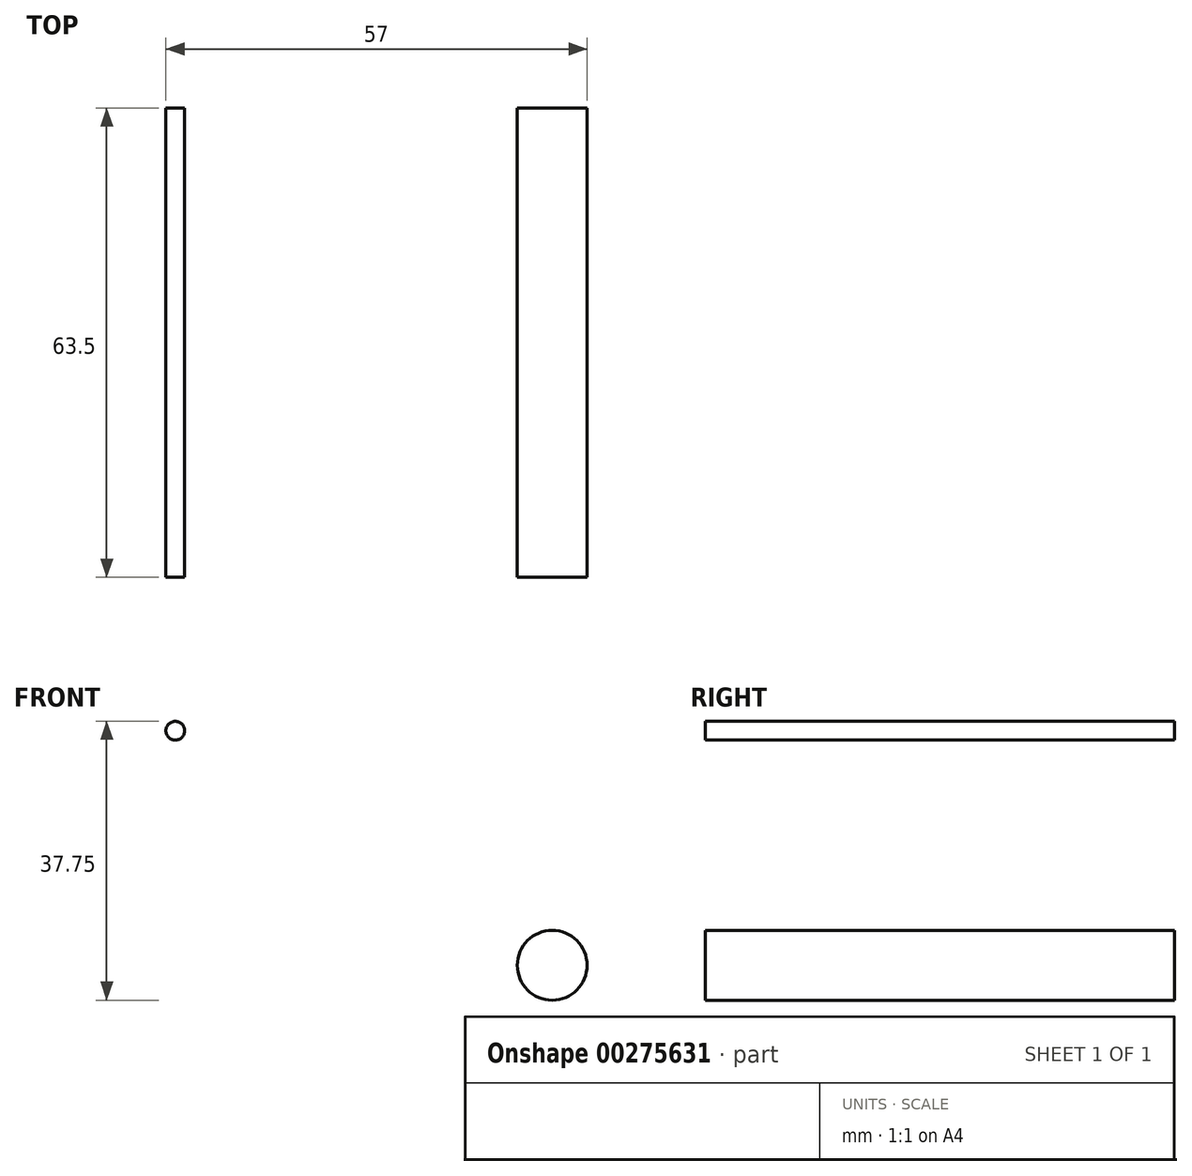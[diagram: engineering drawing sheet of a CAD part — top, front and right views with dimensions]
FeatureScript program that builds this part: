
annotation { "Feature Type Name" : "Feature", "Feature Type Description" : "" }
export const myFeature = defineFeature(function(context is Context, id is Id, definition is map)
    precondition{}
    {
        {
            var Q0;
            Q0=qCreatedBy(makeId("Front.planeOp"),FACE);
            var sketch = newSketch(context, id + "F0", { "sketchPlane" : qUnion([Q0])});
            skCircle(sketch, "E0", {"center": v(0, 0) * mm, "radius": 4.73 * mm});
            skSolve(sketch);
        }
        {
            var Q0;
            Q0=makeQuery(id+"F0.imprint","IMPRINT",FACE,{"disambiguationData":[TD([[makeQuery(id+"F0.imprint","IMPRINT",EDGE,{"derivedFrom":sQuery(id+"F0.wireOp",EDGE,"E0")}),1.0]])]});
            extrude(context, id + "F1", {"entities" : qUnion([Q0]), "depth" : 63.5 * mm});
        }
        {
            var Q0;
            Q0=qCreatedBy(makeId("Front.planeOp"),FACE);
            var sketch = newSketch(context, id + "F2", { "sketchPlane" : qUnion([Q0])});
            skCircle(sketch, "E1", {"center": v(-51, 31.75) * mm, "radius": 1.27 * mm});
            skSolve(sketch);
        }
        {
            var Q0;
            Q0 = qSketchRegion(id + "F2", true);
            extrude(context, id + "F3", {"entities" : qUnion([Q0]), "depth" : 63.5 * mm});
        }
    });
